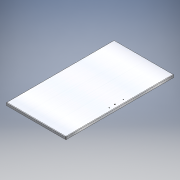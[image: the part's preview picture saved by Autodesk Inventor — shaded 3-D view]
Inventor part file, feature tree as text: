
AUTODESK INVENTOR PART (.ipt)
format: ipt  version: 2017 (Build 210142000, 142)  size: 389,632 bytes
history: native  units: mm
features: sketch x9, sheet_metal_op x8, other x5, hole x2, chamfer x2, plane x1
ambient origin geometry x8: Origin, YZ Plane, XZ Plane, XY Plane, X Axis, Y Axis, Z Axis, Center Point
bodies: Solid1 (feature_tree)
feature tree (27):
  sheet_metal_op  "Face1"
  sheet_metal_op  "Flange1"
  sketch  "Sketch3"  dims[d9=3.0mm]
  hole  "Hole1"  [1 undecoded]
  sheet_metal_op  "Hem1"
  sheet_metal_op  "Hem2"
  sheet_metal_op  "Hem3"
  sheet_metal_op  "Hem4"
  plane  "Work Plane1"
  other  "Decal1"
  chamfer  "Chamfer1"  Distance=1.5mm Angle=90.0deg
  hole  "Hole2"  [1 undecoded]
  chamfer  "Chamfer2"  Distance=100.0mm
  sketch  "Sketch1"  dims[d6=1.5mm d7=1.5mm]
  other  "Plate1"
  sketch  "Sketch2"  dims[d8=0.75mm]
  other  "Plate2"
  sheet_metal_op  "Bend1"
  sheet_metal_op  "Corner1"
  sketch  "Sketch4"  dims[d10=1.5mm d11=20.0mm d12=90.0deg d13=1.5mm]
  sketch  "Sketch9"  dims[d24=25.0mm d26=100.0mm d27=4.5mm d28=6.0mm d29=4.0mm d30=2.0mm d31=90.0deg d32=1.5mm d33=20.594885mm d35=1.5mm d36=0.75mm d37=3.0mm d38=1.5mm d39=10.0mm d40=0.15mm d41=0.075mm d42=1.5mm d43=0.75mm d44=3.0mm d45=1.5mm d46=10.0mm d47=0.15mm d48=0.075mm d49=1.5mm d50=0.75mm d51=3.0mm d52=1.5mm d53=416.0mm d54=10.0mm d55=0.15mm d56=0.075mm d57=1.5mm d58=0.75mm d59=3.0mm d60=1.5mm d61=416.0mm d62=10.0mm d63=0.15mm d64=0.075mm d65=200.0mm d71=1.5mm d72=2.0mm d73=45.0deg d74=423.299mm d75=766.0mm d76=766.0mm d77=423.299mm d78=4.5mm d79=6.0mm d80=4.0mm d81=2.0mm d82=90.0deg d83=1.5mm d84=20.594885mm d85=1.5mm d86=2.0mm d87=45.0deg d88=50.0mm]
  other  "Image1"
  sketch  "Sketch5"  dims[d14=6.0mm d15=1.5mm]
  sketch  "Sketch6"  dims[d16=1.5mm]
  sketch  "Sketch7"  dims[d17=25.0mm]
  sketch  "Sketch8"  dims[d18=373.0mm]
  other  "Definition1"
note: 2 required parameter values undecoded (feature->parameter linkage not recoverable at this tier; creation-order binding heuristic only, values carry confidence <= 0.55)
